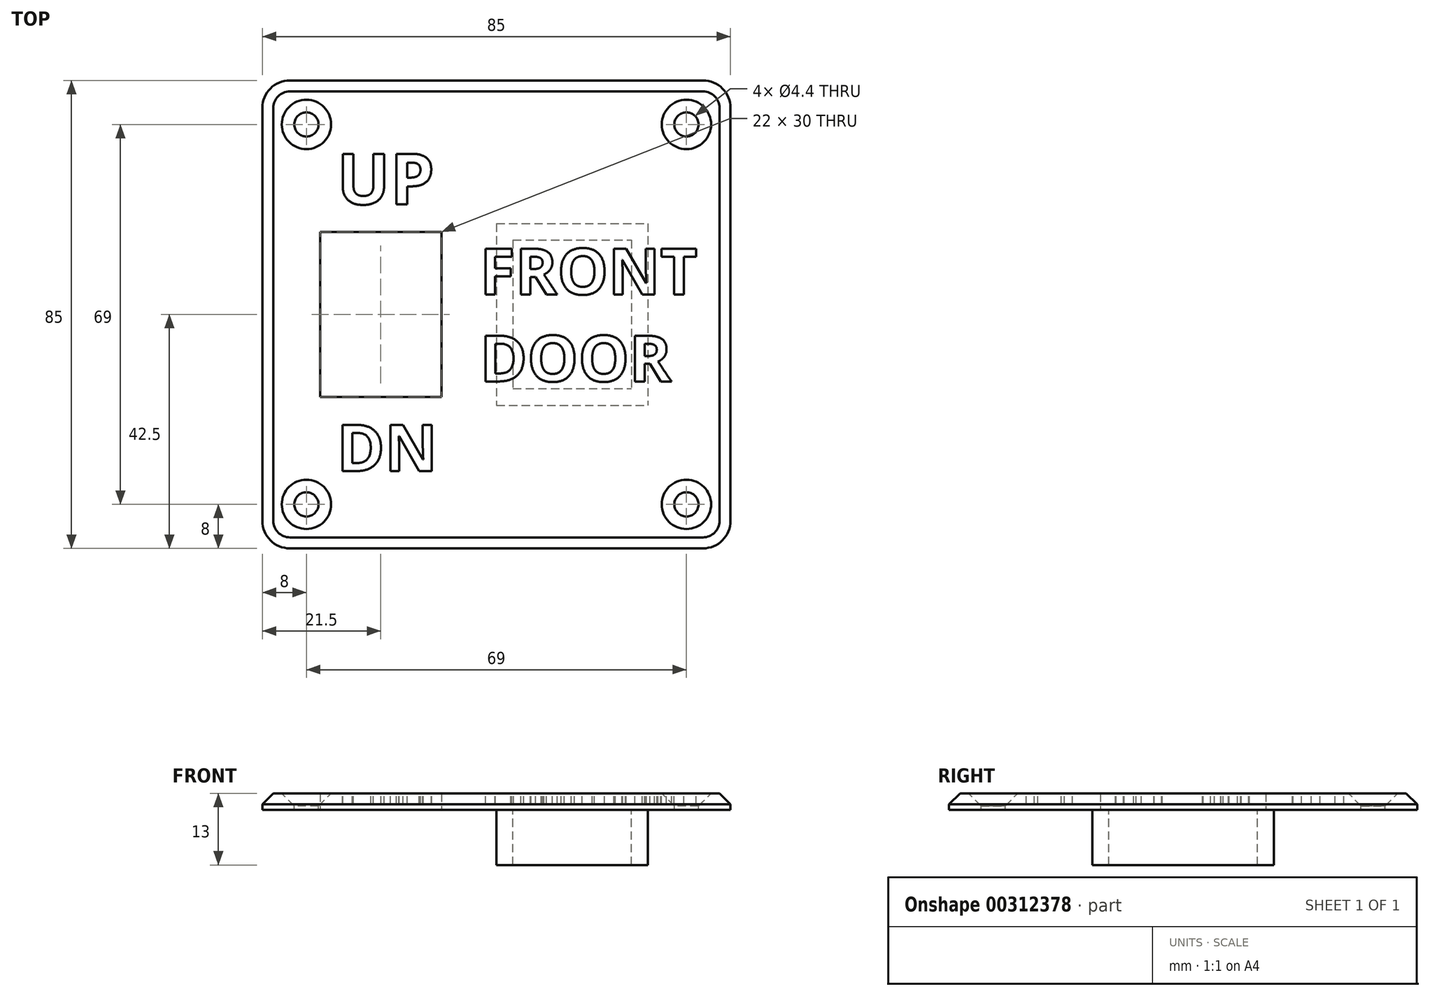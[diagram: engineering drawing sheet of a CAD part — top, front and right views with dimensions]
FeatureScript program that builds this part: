
annotation { "Feature Type Name" : "Feature", "Feature Type Description" : "" }
export const myFeature = defineFeature(function(context is Context, id is Id, definition is map)
    precondition{}
    {
        {
            var Q0;
            Q0=qCreatedBy(makeId("Top.planeOp"),FACE);
            var sketch = newSketch(context, id + "F0", { "sketchPlane" : qUnion([Q0])});
            skLineSegment(sketch, "E0.bottom", {"start": v(-37.5, 42.5) * mm, "end": v(37.5, 42.5) * mm});
            skLineSegment(sketch, "E0.top", {"start": v(-37.5, -42.5) * mm, "end": v(37.5, -42.5) * mm});
            skLineSegment(sketch, "E0.left", {"start": v(-42.5, 37.5) * mm, "end": v(-42.5, -37.5) * mm});
            skLineSegment(sketch, "E0.right", {"start": v(42.5, 37.5) * mm, "end": v(42.5, -37.5) * mm});
            skLineSegment(sketch, "E1.bottom", {"start": v(-32, 15) * mm, "end": v(-10, 15) * mm});
            skLineSegment(sketch, "E1.top", {"start": v(-32, -15) * mm, "end": v(-10, -15) * mm});
            skLineSegment(sketch, "E1.left", {"start": v(-32, 15) * mm, "end": v(-32, -15) * mm});
            skLineSegment(sketch, "E1.right", {"start": v(-10, 15) * mm, "end": v(-10, -15) * mm});
            skCircle(sketch, "E2", {"center": v(34.5, 34.5) * mm, "radius": 2 * mm});
            skLineSegment(sketch, "E3", {"start": v(-42.5, 0) * mm, "end": v(56.67, 0) * mm, "construction": true});
            skLineSegment(sketch, "E4", {"start": v(0, 42.5) * mm, "end": v(0, -77.51) * mm, "construction": true});
            skCircle(sketch, "E5.1.0", {"center": v(-34.5, 34.5) * mm, "radius": 2 * mm});
            skCircle(sketch, "E5.2.0", {"center": v(-34.5, -34.5) * mm, "radius": 2 * mm});
            skCircle(sketch, "E5.3.0", {"center": v(34.5, -34.5) * mm, "radius": 2 * mm});
            skPoint(sketch, "E5.center", {"position": v(0, 0) * mm});
            skLineSegment(sketch, "E6.bottom", {"start": v(3, 13.5) * mm, "end": v(24.5, 13.5) * mm});
            skLineSegment(sketch, "E6.top", {"start": v(3, -13.5) * mm, "end": v(24.5, -13.5) * mm});
            skLineSegment(sketch, "E6.left", {"start": v(3, 13.5) * mm, "end": v(3, -13.5) * mm});
            skLineSegment(sketch, "E6.right", {"start": v(24.5, 13.5) * mm, "end": v(24.5, -13.5) * mm});
            skLineSegment(sketch, "E7.bottom", {"start": v(0, 16.5) * mm, "end": v(27.5, 16.5) * mm});
            skLineSegment(sketch, "E7.top", {"start": v(0, -16.5) * mm, "end": v(27.5, -16.5) * mm});
            skLineSegment(sketch, "E7.left", {"start": v(0, 16.5) * mm, "end": v(0, -16.5) * mm});
            skLineSegment(sketch, "E7.right", {"start": v(27.5, 16.5) * mm, "end": v(27.5, -16.5) * mm});
            skPoint(sketch, "E8.visualSharp", {"position": v(-42.5, 42.5) * mm});
            skArc(sketch, "E8.filletArc", {"start": v(-37.5, 42.5) * mm, "mid": v(-41.04, 41.04) * mm, "end": v(-42.5, 37.5) * mm});
            skPoint(sketch, "E9.visualSharp", {"position": v(42.5, 42.5) * mm});
            skArc(sketch, "E9.filletArc", {"start": v(42.5, 37.5) * mm, "mid": v(41.04, 41.04) * mm, "end": v(37.5, 42.5) * mm});
            skPoint(sketch, "E10.visualSharp", {"position": v(42.5, -42.5) * mm});
            skArc(sketch, "E10.filletArc", {"start": v(37.5, -42.5) * mm, "mid": v(41.04, -41.04) * mm, "end": v(42.5, -37.5) * mm});
            skPoint(sketch, "E11.visualSharp", {"position": v(-42.5, -42.5) * mm});
            skArc(sketch, "E11.filletArc", {"start": v(-42.5, -37.5) * mm, "mid": v(-41.04, -41.04) * mm, "end": v(-37.5, -42.5) * mm});
            skSolve(sketch);
        }
        {
            var Q0;
            Q0=makeQuery(id+"F0.imprint","IMPRINT",FACE,{"disambiguationData":[TD([[makeQuery(id+"F0.imprint","IMPRINT",EDGE,{"derivedFrom":sQuery(id+"F0.wireOp",EDGE,"E0.bottom")}),-1.0]])]});
            extrude(context, id + "F1", {"entities" : qUnion([Q0]), "depth" : 3 * mm});
        }
        {
            var Q0;
            Q0=makeQuery(id+"F0.imprint","IMPRINT",FACE,{"disambiguationData":[TD([[makeQuery(id+"F0.imprint","IMPRINT",EDGE,{"derivedFrom":sQuery(id+"F0.wireOp",EDGE,"E6.bottom")}),1.0]])]});
            var Q1;
            Q1=makeQuery(id+"F1.opExtrude","CAP_FACE",FACE,{"disambiguationData":[OSD([sQuery(id+"F0.wireOp",EDGE,"E0.bottom"),sQuery(id+"F0.wireOp",EDGE,"E0.top"),sQuery(id+"F0.wireOp",EDGE,"E0.left"),sQuery(id+"F0.wireOp",EDGE,"E0.right"),sQuery(id+"F0.wireOp",EDGE,"E1.bottom"),sQuery(id+"F0.wireOp",EDGE,"E1.top"),sQuery(id+"F0.wireOp",EDGE,"E1.left"),sQuery(id+"F0.wireOp",EDGE,"E1.right"),sQuery(id+"F0.wireOp",EDGE,"E2"),sQuery(id+"F0.wireOp",EDGE,"E5.1.0"),sQuery(id+"F0.wireOp",EDGE,"E5.2.0"),sQuery(id+"F0.wireOp",EDGE,"E5.3.0"),sQuery(id+"F0.wireOp",EDGE,"E7.bottom"),sQuery(id+"F0.wireOp",EDGE,"E7.top"),sQuery(id+"F0.wireOp",EDGE,"E7.left"),sQuery(id+"F0.wireOp",EDGE,"E7.right"),sQuery(id+"F0.wireOp",EDGE,"E8.filletArc"),sQuery(id+"F0.wireOp",EDGE,"E9.filletArc"),sQuery(id+"F0.wireOp",EDGE,"E10.filletArc"),sQuery(id+"F0.wireOp",EDGE,"E11.filletArc")])],"isStart":true});
            extrude(context, id + "F2", {"entities" : qUnion([Q0]), "operationType" : NewBodyOperationType.ADD, "oppositeDirection" : true, "endBoundEntityFace" : qUnion([Q1]), "depth" : 10 * mm, "hasSecondDirection" : true, "secondDirectionOppositeDirection" : false, "secondDirectionDepth" : 3 * mm});
        }
        {
            var Q0;
            Q0=makeQuery(id+"F0.imprint","IMPRINT",FACE,{"disambiguationData":[TD([[makeQuery(id+"F0.imprint","IMPRINT",EDGE,{"derivedFrom":sQuery(id+"F0.wireOp",EDGE,"E6.bottom")}),-1.0]])]});
            extrude(context, id + "F3", {"entities" : qUnion([Q0]), "operationType" : NewBodyOperationType.ADD, "depth" : 3 * mm});
        }
        {
            var Q0;
            Q0=makeQuery(id+"F1.opExtrude","CAP_EDGE",EDGE,{"disambiguationData":[OSD([sQuery(id+"F0.wireOp",EDGE,"E0.top")])],"isStart":false});
            chamfer(context, id + "F4", {"entities" : qUnion([Q0]), "width" : 2 * mm, "tangentPropagation" : true});
        }
        {
            var Q0;
            {var subQ0=sQuery(id+"F0.wireOp",EDGE,"E6.right");var subQ1=sQuery(id+"F0.wireOp",EDGE,"E6.left");var subQ2=sQuery(id+"F0.wireOp",EDGE,"E6.top");var subQ3=sQuery(id+"F0.wireOp",EDGE,"E6.bottom");var subQ4=sQuery(id+"F0.wireOp",EDGE,"E7.right");var subQ5=sQuery(id+"F0.wireOp",EDGE,"E7.left");var subQ6=sQuery(id+"F0.wireOp",EDGE,"E7.top");var subQ7=sQuery(id+"F0.wireOp",EDGE,"E7.bottom");Q0=makeQuery(id+"F3.boolean.opBoolean","MERGE",FACE,{"derivedFrom":[makeQuery(id+"F2.boolean.opBoolean","MERGE",FACE,{"derivedFrom":[makeQuery(id+"F1.opExtrude","CAP_FACE",FACE,{"disambiguationData":[OSD([sQuery(id+"F0.wireOp",EDGE,"E0.bottom"),sQuery(id+"F0.wireOp",EDGE,"E0.top"),sQuery(id+"F0.wireOp",EDGE,"E0.left"),sQuery(id+"F0.wireOp",EDGE,"E0.right"),sQuery(id+"F0.wireOp",EDGE,"E1.bottom"),sQuery(id+"F0.wireOp",EDGE,"E1.top"),sQuery(id+"F0.wireOp",EDGE,"E1.left"),sQuery(id+"F0.wireOp",EDGE,"E1.right"),sQuery(id+"F0.wireOp",EDGE,"E2"),sQuery(id+"F0.wireOp",EDGE,"E5.1.0"),sQuery(id+"F0.wireOp",EDGE,"E5.2.0"),sQuery(id+"F0.wireOp",EDGE,"E5.3.0"),subQ7,subQ6,subQ5,subQ4,sQuery(id+"F0.wireOp",EDGE,"E8.filletArc"),sQuery(id+"F0.wireOp",EDGE,"E9.filletArc"),sQuery(id+"F0.wireOp",EDGE,"E10.filletArc"),sQuery(id+"F0.wireOp",EDGE,"E11.filletArc")])],"isStart":false}),makeQuery(id+"F2.opExtrude","CAP_FACE",FACE,{"disambiguationData":[OSD([subQ3,subQ2,subQ1,subQ0,subQ7,subQ6,subQ5,subQ4])],"isStart":true})]}),makeQuery(id+"F3.opExtrude","CAP_FACE",FACE,{"disambiguationData":[OSD([subQ3,subQ2,subQ1,subQ0])],"isStart":false})]});}
            var sketch = newSketch(context, id + "F5", { "sketchPlane" : qUnion([Q0])});
            skText(sketch, "E12", { "text": "UP", "fontName": "OpenSans-Bold.ttf"});
            skText(sketch, "E13", { "text": "DN", "fontName": "OpenSans-Bold.ttf"});
            skText(sketch, "E14", { "text": "FRONT\nDOOR", "fontName": "OpenSans-Bold.ttf"});
            const initialGuessF5  = {"E12": [-0.029, 0.02, 1, 0, 0.00923], "E13": [-0.029, -0.02848, 1, 0, 0.00848], "E14": [-0.003, 0.00363, 1, 0, 0.00837]};
            skSetInitialGuess(sketch, initialGuessF5);
            skSolve(sketch);
        }
        {
            var Q0;
            Q0 = qSketchRegion(id + "F5", true);
            extrude(context, id + "F6", {"entities" : qUnion([Q0]), "operationType" : NewBodyOperationType.REMOVE, "oppositeDirection" : true, "depth" : 2 * mm});
        }
        {
            var Q0;
            {var subQ0=sQuery(id+"F0.wireOp",EDGE,"E10.filletArc");var subQ1=sQuery(id+"F0.wireOp",EDGE,"E9.filletArc");var subQ2=sQuery(id+"F0.wireOp",EDGE,"E5.2.0");var subQ3=sQuery(id+"F0.wireOp",EDGE,"E8.filletArc");var subQ4=sQuery(id+"F0.wireOp",EDGE,"E0.right");var subQ5=sQuery(id+"F0.wireOp",EDGE,"E0.left");var subQ6=sQuery(id+"F0.wireOp",EDGE,"E1.right");var subQ7=sQuery(id+"F0.wireOp",EDGE,"E0.bottom");var subQ8=sQuery(id+"F0.wireOp",EDGE,"E1.left");var subQ9=sQuery(id+"F0.wireOp",EDGE,"E1.top");var subQ10=sQuery(id+"F0.wireOp",EDGE,"E11.filletArc");var subQ11=sQuery(id+"F0.wireOp",EDGE,"E1.bottom");var subQ12=sQuery(id+"F0.wireOp",EDGE,"E2");var subQ13=sQuery(id+"F0.wireOp",EDGE,"E0.top");var subQ14=sQuery(id+"F0.wireOp",EDGE,"E5.1.0");var subQ15=sQuery(id+"F0.wireOp",EDGE,"E5.3.0");var subQ16=sQuery(id+"F0.wireOp",EDGE,"E6.right");var subQ17=sQuery(id+"F0.wireOp",EDGE,"E6.left");var subQ18=sQuery(id+"F0.wireOp",EDGE,"E6.top");var subQ19=sQuery(id+"F0.wireOp",EDGE,"E6.bottom");var subQ20=sQuery(id+"F0.wireOp",EDGE,"E7.right");var subQ21=sQuery(id+"F0.wireOp",EDGE,"E7.left");var subQ22=sQuery(id+"F0.wireOp",EDGE,"E7.top");var subQ23=sQuery(id+"F0.wireOp",EDGE,"E7.bottom");Q0=makeQuery(id+"F6.boolean.opBoolean","SPLIT",FACE,{"disambiguationData":[TD([makeQuery(id+"F1.opExtrude","SWEPT_FACE",FACE,{"disambiguationData":[OSD([subQ11])]})])],"derivedFrom":makeQuery(id+"F3.boolean.opBoolean","MERGE",FACE,{"derivedFrom":[makeQuery(id+"F2.boolean.opBoolean","MERGE",FACE,{"derivedFrom":[makeQuery(id+"F1.opExtrude","CAP_FACE",FACE,{"disambiguationData":[OSD([subQ7,subQ13,subQ5,subQ4,subQ11,subQ9,subQ8,subQ6,subQ12,subQ14,subQ2,subQ15,subQ23,subQ22,subQ21,subQ20,subQ3,subQ1,subQ0,subQ10])],"isStart":false}),makeQuery(id+"F2.opExtrude","CAP_FACE",FACE,{"disambiguationData":[OSD([subQ19,subQ18,subQ17,subQ16,subQ23,subQ22,subQ21,subQ20])],"isStart":true})]}),makeQuery(id+"F3.opExtrude","CAP_FACE",FACE,{"disambiguationData":[OSD([subQ19,subQ18,subQ17,subQ16])],"isStart":false})]})});}
            var sketch = newSketch(context, id + "F7", { "sketchPlane" : qUnion([Q0])});
            skPoint(sketch, "E15", {"position": v(-34.5, 34.5) * mm});
            skPoint(sketch, "E16", {"position": v(34.5, 34.5) * mm});
            skPoint(sketch, "E17", {"position": v(34.5, -34.5) * mm});
            skPoint(sketch, "E18", {"position": v(-34.5, -34.5) * mm});
            skSolve(sketch);
        }
        {
            var Q0;
            Q0=sQuery(id+"F7.wireOp",VERTEX,"E15");
            var Q1;
            Q1=sQuery(id+"F7.wireOp",VERTEX,"E16");
            var Q2;
            Q2=sQuery(id+"F7.wireOp",VERTEX,"E17");
            var Q3;
            Q3=sQuery(id+"F7.wireOp",VERTEX,"E18");
            var Q4;
            Q4=makeQuery(id+"F1.opExtrude","SWEPT_BODY",BODY,{"disambiguationData":[OSD([sQuery(id+"F0.wireOp",EDGE,"E0.bottom"),sQuery(id+"F0.wireOp",EDGE,"E0.top"),sQuery(id+"F0.wireOp",EDGE,"E0.left"),sQuery(id+"F0.wireOp",EDGE,"E0.right"),sQuery(id+"F0.wireOp",EDGE,"E1.bottom"),sQuery(id+"F0.wireOp",EDGE,"E1.top"),sQuery(id+"F0.wireOp",EDGE,"E1.left"),sQuery(id+"F0.wireOp",EDGE,"E1.right"),sQuery(id+"F0.wireOp",EDGE,"E2"),sQuery(id+"F0.wireOp",EDGE,"E5.1.0"),sQuery(id+"F0.wireOp",EDGE,"E5.2.0"),sQuery(id+"F0.wireOp",EDGE,"E5.3.0"),sQuery(id+"F0.wireOp",EDGE,"E7.bottom"),sQuery(id+"F0.wireOp",EDGE,"E7.top"),sQuery(id+"F0.wireOp",EDGE,"E7.left"),sQuery(id+"F0.wireOp",EDGE,"E7.right"),sQuery(id+"F0.wireOp",EDGE,"E8.filletArc"),sQuery(id+"F0.wireOp",EDGE,"E9.filletArc"),sQuery(id+"F0.wireOp",EDGE,"E10.filletArc"),sQuery(id+"F0.wireOp",EDGE,"E11.filletArc")])]});
            hole(context, id + "F8", {"style" : HoleStyle.C_SINK, "endStyle" : HoleEndStyle.THROUGH, "standardTappedOrClearance" : lookupTablePath({ "standard" : "ISO", "fit" : "Normal", "size" : "M4", "type" : "Clearance" }), "standardBlindInLast" : lookupTablePath({ "fit" : "Standard", "standard" : "ISO", "size" : "M4", "type" : "Clearance" }), "holeDiameter" : 4.4 * mm, "cSinkDiameter" : 8.96 * mm, "cSinkAngle" : 90 * degree, "tappedDepth" : 12 * mm, "tapClearance" : 3, "locations" : qUnion([Q0, Q1, Q2, Q3]), "scope" : qUnion([Q4])});
        }
    });
